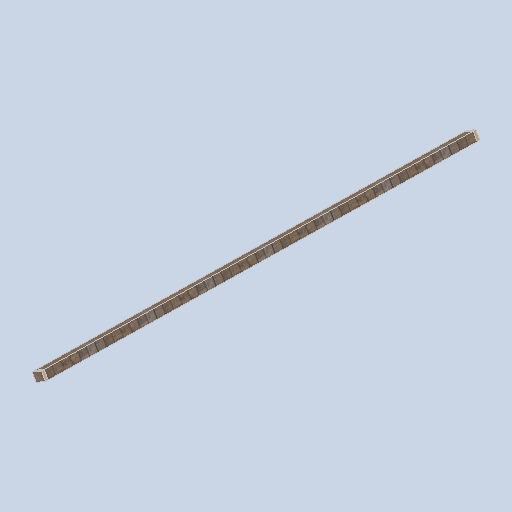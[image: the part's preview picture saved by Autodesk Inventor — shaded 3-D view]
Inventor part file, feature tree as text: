
AUTODESK INVENTOR PART (.ipt)
format: ipt  version: 2024.2 (Build 282272000, 272)  size: 310,784 bytes
history: native  units: mm
features: sketch x4, plane x2, extrude x2, projected_geometry x2, loft x1
ambient origin geometry x8: Origin, YZ Plane, XZ Plane, XY Plane, X Axis, Y Axis, Z Axis, Center Point
bodies: Solid1 (feature_tree)
feature tree (11):
  sketch  "Sketch1"  dims[d0=0.0mm d1=8101.0mm d2=0.0mm d3=90.0deg]
  plane  "Work Plane2"
  loft  "Loft1"
  sketch  "Sketch3"  dims[d8=50.0mm d9=0.0mm]
  sketch  "Sketch4"
  extrude  "Extrusion1"  Depth=50.0mm TaperAngle=0.0deg
  extrude  "Extrusion2"  [1 undecoded]
  plane  "Work Plane1"
  sketch  "Sketch2"  dims[d4=0.0mm d5=90.0deg d6=50.0mm d7=0.0mm]
  projected_geometry  "Projected Loop1"
  projected_geometry  "Projected Loop2"
note: 1 required parameter value undecoded (feature->parameter linkage not recoverable at this tier; creation-order binding heuristic only, values carry confidence <= 0.55)
